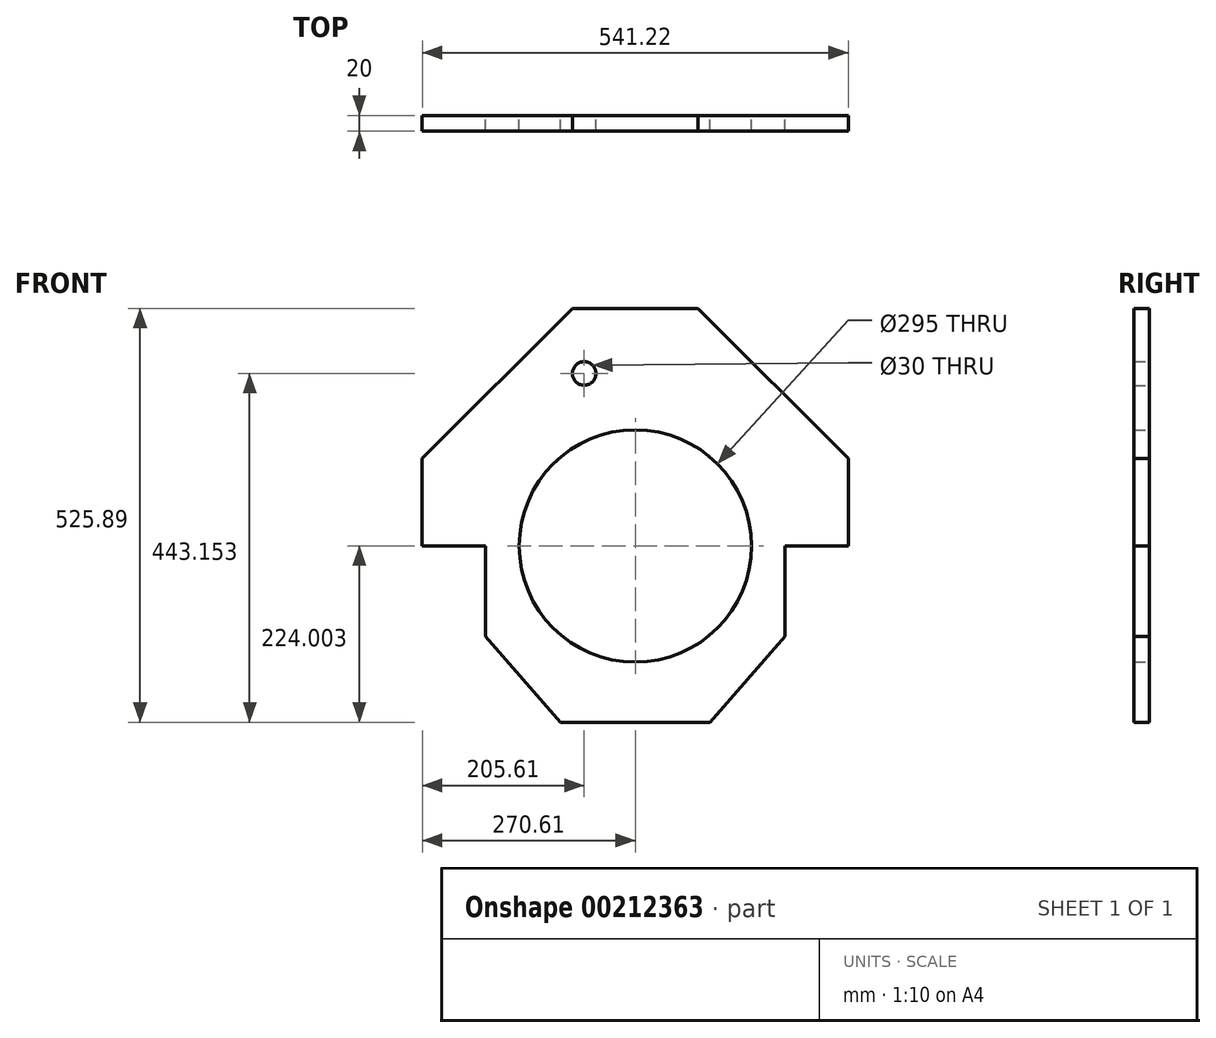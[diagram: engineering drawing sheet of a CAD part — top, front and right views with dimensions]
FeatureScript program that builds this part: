
annotation { "Feature Type Name" : "Feature", "Feature Type Description" : "" }
export const myFeature = defineFeature(function(context is Context, id is Id, definition is map)
    precondition{}
    {
        {
            var Q0;
            Q0=qCreatedBy(makeId("Front.planeOp"),FACE);
            var sketch = newSketch(context, id + "F0", { "sketchPlane" : qUnion([Q0])});
            skCircle(sketch, "E0", {"center": v(0, -64.78) * mm, "radius": 80 * mm});
            skCircle(sketch, "E1", {"center": v(0, -64.78) * mm, "radius": 10 * mm});
            skLineSegment(sketch, "E2", {"start": v(230, -64.78) * mm, "end": v(-230, -64.78) * mm});
            skCircle(sketch, "E3", {"center": v(0, -64.78) * mm, "radius": 147.5 * mm});
            skCircle(sketch, "E4", {"center": v(0, -64.78) * mm, "radius": 30 * mm});
            skCircle(sketch, "E5", {"center": v(-65, 154.37) * mm, "radius": 60 * mm});
            skCircle(sketch, "E6", {"center": v(-65, 154.37) * mm, "radius": 15 * mm});
            skLineSegment(sketch, "E7", {"start": v(-190, -179.78) * mm, "end": v(-94.8, -288.78) * mm});
            skLineSegment(sketch, "E8", {"start": v(-190, -34.26) * mm, "end": v(-190, -179.78) * mm});
            skLineSegment(sketch, "E9", {"start": v(-190, -34.26) * mm, "end": v(-270.61, 46.36) * mm});
            skLineSegment(sketch, "E10", {"start": v(-270.61, 46.36) * mm, "end": v(-79.86, 237.11) * mm});
            skLineSegment(sketch, "E11", {"start": v(-79.86, 237.11) * mm, "end": v(0, 237.11) * mm});
            skLineSegment(sketch, "E12", {"start": v(0, -288.78) * mm, "end": v(-94.8, -288.78) * mm});
            skLineSegment(sketch, "E13", {"start": v(79.86, 237.11) * mm, "end": v(0, 237.11) * mm});
            skLineSegment(sketch, "E14", {"start": v(270.61, 46.36) * mm, "end": v(79.86, 237.11) * mm});
            skLineSegment(sketch, "E15", {"start": v(190, -34.26) * mm, "end": v(270.61, 46.36) * mm});
            skLineSegment(sketch, "E16", {"start": v(190, -34.26) * mm, "end": v(190, -179.78) * mm});
            skLineSegment(sketch, "E17", {"start": v(190, -179.78) * mm, "end": v(94.8, -288.78) * mm});
            skLineSegment(sketch, "E18", {"start": v(0, -288.78) * mm, "end": v(94.8, -288.78) * mm});
            skCircle(sketch, "E19", {"center": v(65, 154.37) * mm, "radius": 15 * mm});
            skCircle(sketch, "E20", {"center": v(65, 154.37) * mm, "radius": 60 * mm});
            skLineSegment(sketch, "E21", {"start": v(0, -64.78) * mm, "end": v(353.55, 288.78) * mm});
            skLineSegment(sketch, "E22", {"start": v(0, -64.78) * mm, "end": v(-353.55, 288.78) * mm});
            skLineSegment(sketch, "E23", {"start": v(270.61, 46.36) * mm, "end": v(270.61, -64.78) * mm});
            skLineSegment(sketch, "E24", {"start": v(230, -64.78) * mm, "end": v(270.61, -64.78) * mm});
            skLineSegment(sketch, "E25", {"start": v(-270.61, 46.36) * mm, "end": v(-270.61, -64.78) * mm});
            skLineSegment(sketch, "E26", {"start": v(-270.61, -64.78) * mm, "end": v(-230, -64.78) * mm});
            skSolve(sketch);
        }
        {
            var Q0;
            {var subQ0=sQuery(id+"F0.wireOp",EDGE,"E9");Q0=makeQuery(id+"F0.imprint","IMPRINT",FACE,{"disambiguationData":[TD([[makeQuery(id+"F0.imprint","IMPRINT",EDGE,{"derivedFrom":subQ0}),-1.0]])]});}
            var Q1;
            {var subQ0=sQuery(id+"F0.wireOp",EDGE,"E7");Q1=makeQuery(id+"F0.imprint","IMPRINT",FACE,{"disambiguationData":[TD([[makeQuery(id+"F0.imprint","IMPRINT",EDGE,{"derivedFrom":subQ0}),1.0]])]});}
            var Q2;
            {var subQ0=sQuery(id+"F0.wireOp",EDGE,"E15");Q2=makeQuery(id+"F0.imprint","IMPRINT",FACE,{"disambiguationData":[TD([[makeQuery(id+"F0.imprint","IMPRINT",EDGE,{"derivedFrom":subQ0}),1.0]])]});}
            var Q3;
            Q3=makeQuery(id+"F0.imprint","IMPRINT",FACE,{"disambiguationData":[TD([[makeQuery(id+"F0.imprint","IMPRINT",EDGE,{"derivedFrom":sQuery(id+"F0.wireOp",EDGE,"E5")}),1.0]])]});
            var Q4;
            Q4=makeQuery(id+"F0.imprint","IMPRINT",FACE,{"disambiguationData":[TD([[makeQuery(id+"F0.imprint","IMPRINT",EDGE,{"derivedFrom":sQuery(id+"F0.wireOp",EDGE,"E5")}),-1.0]])]});
            var Q5;
            Q5=makeQuery(id+"F0.imprint","IMPRINT",FACE,{"disambiguationData":[TD([[makeQuery(id+"F0.imprint","IMPRINT",EDGE,{"derivedFrom":sQuery(id+"F0.wireOp",EDGE,"E6")}),-1.0]])]});
            var Q6;
            Q6=makeQuery(id+"F0.imprint","IMPRINT",FACE,{"disambiguationData":[TD([[makeQuery(id+"F0.imprint","IMPRINT",EDGE,{"derivedFrom":sQuery(id+"F0.wireOp",EDGE,"E19")}),1.0]])]});
            var Q7;
            Q7=makeQuery(id+"F0.imprint","IMPRINT",FACE,{"disambiguationData":[TD([[makeQuery(id+"F0.imprint","IMPRINT",EDGE,{"derivedFrom":sQuery(id+"F0.wireOp",EDGE,"E19")}),-1.0]])]});
            extrude(context, id + "F1", {"entities" : qUnion([Q0, Q1, Q2, Q3, Q4, Q5, Q6, Q7]), "depth" : 20 * mm});
        }
        {
            var Q0;
            {var subQ1=sQuery(id+"F0.wireOp",EDGE,"E15");Q0=makeQuery(id+"F0.imprint","IMPRINT",FACE,{"disambiguationData":[TD([[makeQuery(id+"F0.imprint","IMPRINT",EDGE,{"derivedFrom":subQ1}),-1.0]])]});}
            var Q1;
            {var subQ0=sQuery(id+"F0.wireOp",EDGE,"E9");Q1=makeQuery(id+"F0.imprint","IMPRINT",FACE,{"disambiguationData":[TD([[makeQuery(id+"F0.imprint","IMPRINT",EDGE,{"derivedFrom":subQ0}),1.0]])]});}
            extrude(context, id + "F2", {"entities" : qUnion([Q0, Q1]), "operationType" : NewBodyOperationType.ADD, "depth" : 20 * mm});
        }
    });
